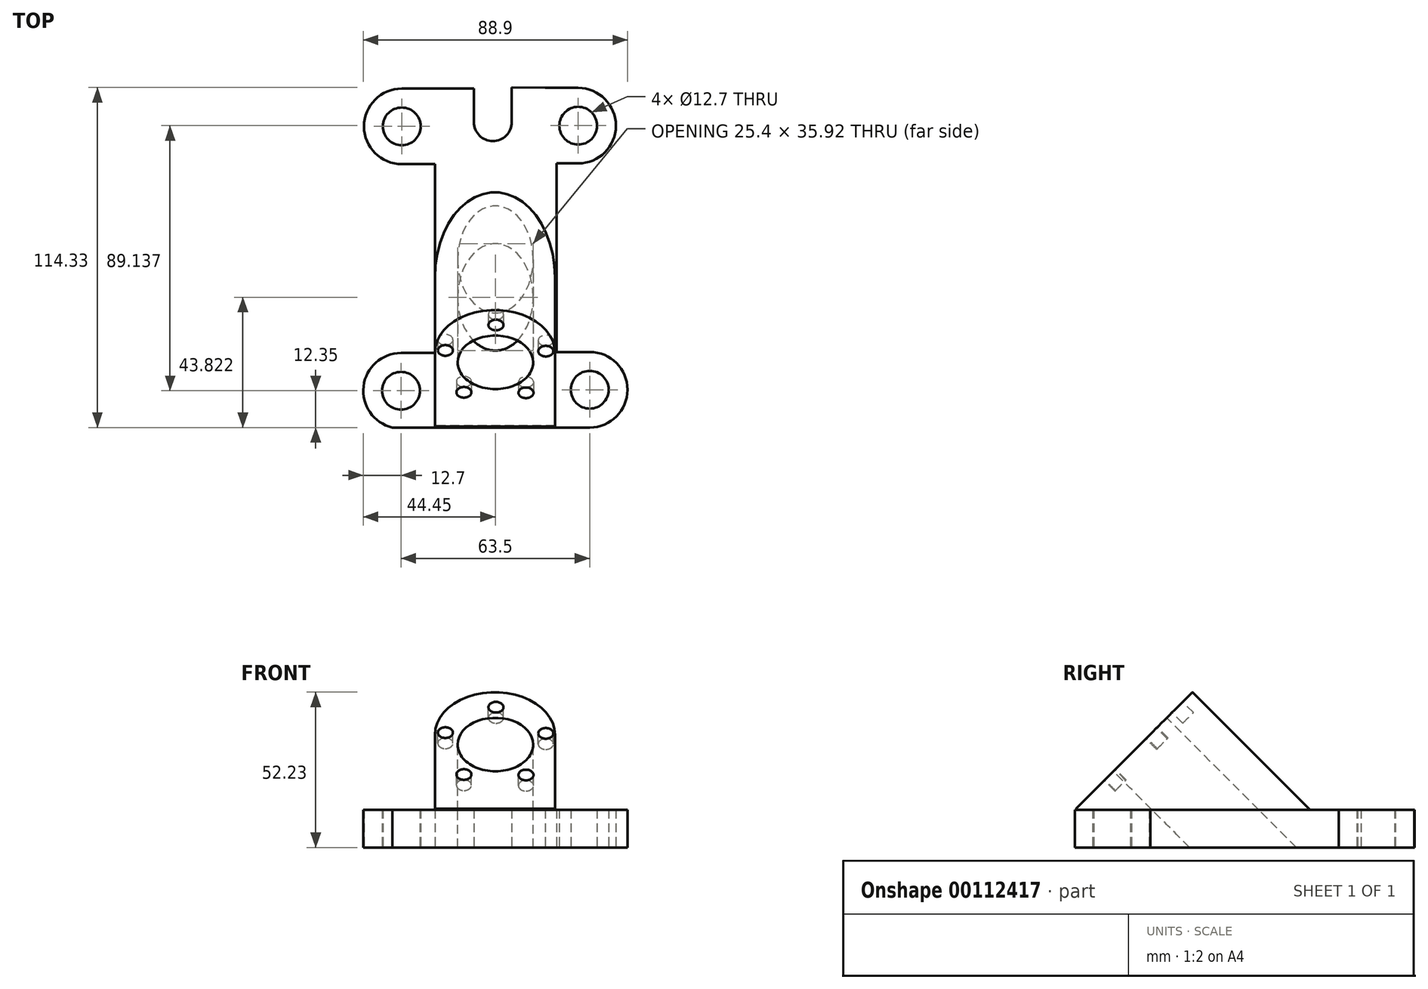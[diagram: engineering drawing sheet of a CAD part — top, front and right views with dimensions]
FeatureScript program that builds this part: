
annotation { "Feature Type Name" : "Feature", "Feature Type Description" : "" }
export const myFeature = defineFeature(function(context is Context, id is Id, definition is map)
    precondition{}
    {
        {
            var Q0;
            Q0=qCreatedBy(makeId("Top.planeOp"),FACE);
            var sketch = newSketch(context, id + "F0", { "sketchPlane" : qUnion([Q0])});
            skLineSegment(sketch, "E0.bottom", {"start": v(0, 0) * mm, "end": v(40.88, 0) * mm});
            skLineSegment(sketch, "E1", {"start": v(0, 113.95) * mm, "end": v(-11.15, 113.95) * mm});
            skLineSegment(sketch, "E2", {"start": v(-11.15, 113.95) * mm, "end": v(-11.15, 88.55) * mm});
            skLineSegment(sketch, "E3", {"start": v(-11.15, 88.55) * mm, "end": v(0, 88.55) * mm});
            skLineSegment(sketch, "E4", {"start": v(0, 0) * mm, "end": v(-14.37, 0) * mm});
            skLineSegment(sketch, "E5", {"start": v(-11.41, 25.05) * mm, "end": v(0, 25.05) * mm});
            skLineSegment(sketch, "E6", {"start": v(40.88, 0) * mm, "end": v(52.09, 0) * mm});
            skLineSegment(sketch, "E7", {"start": v(52.09, 25.4) * mm, "end": v(40.88, 25.4) * mm});
            skLineSegment(sketch, "E8", {"start": v(37.1, 114.19) * mm, "end": v(48.21, 114.19) * mm});
            skLineSegment(sketch, "E9", {"start": v(48.21, 114.19) * mm, "end": v(48.21, 88.79) * mm});
            skLineSegment(sketch, "E10", {"start": v(48.21, 88.79) * mm, "end": v(40.88, 88.79) * mm});
            skArc(sketch, "E11", {"start": v(-11.15, 113.95) * mm, "mid": v(-23.85, 101.25) * mm, "end": v(-11.15, 88.55) * mm});
            skArc(sketch, "E12", {"start": v(-11.41, 25.05) * mm, "mid": v(-24.02, 13.84) * mm, "end": v(-14.37, 0) * mm});
            skArc(sketch, "E13", {"start": v(52.09, 0) * mm, "mid": v(64.79, 12.7) * mm, "end": v(52.09, 25.4) * mm});
            skArc(sketch, "E14", {"start": v(48.21, 88.79) * mm, "mid": v(60.91, 101.49) * mm, "end": v(48.21, 114.19) * mm});
            skCircle(sketch, "E15", {"center": v(-11.41, 12.35) * mm, "radius": 6.35 * mm});
            skCircle(sketch, "E16", {"center": v(52.09, 12.7) * mm, "radius": 6.35 * mm});
            skCircle(sketch, "E17", {"center": v(48.21, 101.49) * mm, "radius": 6.35 * mm});
            skCircle(sketch, "E18", {"center": v(-11.15, 101.25) * mm, "radius": 6.35 * mm});
            skLineSegment(sketch, "E19", {"start": v(0, 88.55) * mm, "end": v(0, 0) * mm});
            skLineSegment(sketch, "E20", {"start": v(40.88, 88.79) * mm, "end": v(40.88, 0) * mm});
            skLineSegment(sketch, "E21", {"start": v(0, 113.95) * mm, "end": v(13.13, 113.95) * mm});
            skLineSegment(sketch, "E22", {"start": v(13.13, 113.95) * mm, "end": v(13.13, 102.64) * mm});
            skLineSegment(sketch, "E23", {"start": v(25.82, 102.64) * mm, "end": v(25.82, 114.33) * mm});
            skLineSegment(sketch, "E24", {"start": v(25.82, 114.33) * mm, "end": v(37.1, 114.19) * mm});
            skArc(sketch, "E25", {"start": v(13.13, 102.64) * mm, "mid": v(19.48, 96.3) * mm, "end": v(25.82, 102.64) * mm});
            skSolve(sketch);
        }
        {
            var Q0;
            Q0 = qSketchRegion(id + "F0", true);
            extrude(context, id + "F1", {"entities" : qUnion([Q0]), "depth" : 12.7 * mm});
        }
        {
            var Q0;
            Q0=makeQuery(id+"F1.opExtrude","CAP_EDGE",EDGE,{"disambiguationData":[OSD([sQuery(id+"F0.wireOp",EDGE,"E0.bottom"),sQuery(id+"F0.wireOp",EDGE,"E4"),sQuery(id+"F0.wireOp",EDGE,"E6")])],"isStart":false});
            cPlane(context, id + "F2", {"entities" : qUnion([Q0]), "cplaneType" : CPlaneType.LINE_ANGLE, "offset" : 25.4 * mm, "angle" : 45 * degree, "width" : 152.4 * mm, "height" : 152.4 * mm});
        }
        {
            var Q0;
            Q0=qCreatedBy(id+"F2.planeOp",FACE);
            var sketch = newSketch(context, id + "F3", { "sketchPlane" : qUnion([Q0])});
            skLineSegment(sketch, "E26", {"start": v(0, 9.43) * mm, "end": v(40.37, 9.43) * mm});
            skLineSegment(sketch, "E27", {"start": v(0, 9.43) * mm, "end": v(0, 44.7) * mm});
            skLineSegment(sketch, "E28", {"start": v(0, 44.7) * mm, "end": v(40.37, 44.7) * mm});
            skLineSegment(sketch, "E29", {"start": v(40.37, 44.7) * mm, "end": v(40.37, 9.43) * mm});
            skArc(sketch, "E30", {"start": v(40.37, 44.7) * mm, "mid": v(20.19, 64.9) * mm, "end": v(0, 44.7) * mm});
            skSolve(sketch);
        }
        {
            var Q0;
            Q0 = qSketchRegion(id + "F3", true);
            var Q1;
            Q1=makeQuery(id+"F1.opExtrude","CAP_FACE",FACE,{"disambiguationData":[OSD([sQuery(id+"F0.wireOp",EDGE,"E0.bottom"),sQuery(id+"F0.wireOp",EDGE,"E1"),sQuery(id+"F0.wireOp",EDGE,"E3"),sQuery(id+"F0.wireOp",EDGE,"E4"),sQuery(id+"F0.wireOp",EDGE,"E5"),sQuery(id+"F0.wireOp",EDGE,"E6"),sQuery(id+"F0.wireOp",EDGE,"E7"),sQuery(id+"F0.wireOp",EDGE,"E8"),sQuery(id+"F0.wireOp",EDGE,"E10"),sQuery(id+"F0.wireOp",EDGE,"E11"),sQuery(id+"F0.wireOp",EDGE,"E12"),sQuery(id+"F0.wireOp",EDGE,"E13"),sQuery(id+"F0.wireOp",EDGE,"E14"),sQuery(id+"F0.wireOp",EDGE,"E15"),sQuery(id+"F0.wireOp",EDGE,"E16"),sQuery(id+"F0.wireOp",EDGE,"E17"),sQuery(id+"F0.wireOp",EDGE,"E18"),sQuery(id+"F0.wireOp",EDGE,"E19"),sQuery(id+"F0.wireOp",EDGE,"E20"),sQuery(id+"F0.wireOp",EDGE,"E21"),sQuery(id+"F0.wireOp",EDGE,"E22"),sQuery(id+"F0.wireOp",EDGE,"E23"),sQuery(id+"F0.wireOp",EDGE,"E24"),sQuery(id+"F0.wireOp",EDGE,"E25")])],"isStart":false});
            var Q2;
            Q2=makeQuery(id+"F1.opExtrude","CAP_FACE",FACE,{"disambiguationData":[OSD([sQuery(id+"F0.wireOp",EDGE,"E0.bottom"),sQuery(id+"F0.wireOp",EDGE,"E1"),sQuery(id+"F0.wireOp",EDGE,"E3"),sQuery(id+"F0.wireOp",EDGE,"E4"),sQuery(id+"F0.wireOp",EDGE,"E5"),sQuery(id+"F0.wireOp",EDGE,"E6"),sQuery(id+"F0.wireOp",EDGE,"E7"),sQuery(id+"F0.wireOp",EDGE,"E8"),sQuery(id+"F0.wireOp",EDGE,"E10"),sQuery(id+"F0.wireOp",EDGE,"E11"),sQuery(id+"F0.wireOp",EDGE,"E12"),sQuery(id+"F0.wireOp",EDGE,"E13"),sQuery(id+"F0.wireOp",EDGE,"E14"),sQuery(id+"F0.wireOp",EDGE,"E15"),sQuery(id+"F0.wireOp",EDGE,"E16"),sQuery(id+"F0.wireOp",EDGE,"E17"),sQuery(id+"F0.wireOp",EDGE,"E18"),sQuery(id+"F0.wireOp",EDGE,"E19"),sQuery(id+"F0.wireOp",EDGE,"E20"),sQuery(id+"F0.wireOp",EDGE,"E21"),sQuery(id+"F0.wireOp",EDGE,"E22"),sQuery(id+"F0.wireOp",EDGE,"E23"),sQuery(id+"F0.wireOp",EDGE,"E24"),sQuery(id+"F0.wireOp",EDGE,"E25")])],"isStart":true});
            extrude(context, id + "F4", {"entities" : qUnion([Q0]), "endBound" : BoundingType.UP_TO_SURFACE, "oppositeDirection" : true, "endBoundEntityFace" : qUnion([Q1]), "depth" : 15.98 * mm});
        }
        {
            var Q0;
            Q0=qCreatedBy(id+"F2.planeOp",FACE);
            var sketch = newSketch(context, id + "F5", { "sketchPlane" : qUnion([Q0])});
            skCircle(sketch, "E31", {"center": v(20.34, 39.97) * mm, "radius": 12.7 * mm, "construction": true});
            skCircle(sketch, "E32", {"center": v(20.52, 57.73) * mm, "radius": 2.54 * mm});
            skCircle(sketch, "E33.1.0", {"center": v(3.5, 45.63) * mm, "radius": 2.54 * mm});
            skCircle(sketch, "E33.2.0", {"center": v(9.75, 25.7) * mm, "radius": 2.54 * mm});
            skCircle(sketch, "E33.3.0", {"center": v(30.63, 25.5) * mm, "radius": 2.54 * mm});
            skCircle(sketch, "E33.4.0", {"center": v(37.29, 45.28) * mm, "radius": 2.54 * mm});
            skSolve(sketch);
        }
        {
            var Q0;
            Q0=qCreatedBy(id+"F2.planeOp",FACE);
            var sketch = newSketch(context, id + "F6", { "sketchPlane" : qUnion([Q0])});
            skCircle(sketch, "E34", {"center": v(20.34, 39.97) * mm, "radius": 12.7 * mm});
            skSolve(sketch);
        }
        {
            var Q0;
            Q0 = qSketchRegion(id + "F5", true);
            extrude(context, id + "F7", {"entities" : qUnion([Q0]), "operationType" : NewBodyOperationType.REMOVE, "oppositeDirection" : true, "depth" : 5.08 * mm});
        }
        {
            var Q0;
            Q0 = qSketchRegion(id + "F6", true);
            extrude(context, id + "F8", {"entities" : qUnion([Q0]), "operationType" : NewBodyOperationType.REMOVE, "endBound" : BoundingType.THROUGH_ALL, "oppositeDirection" : true, "depth" : 25.4 * mm});
        }
    });
